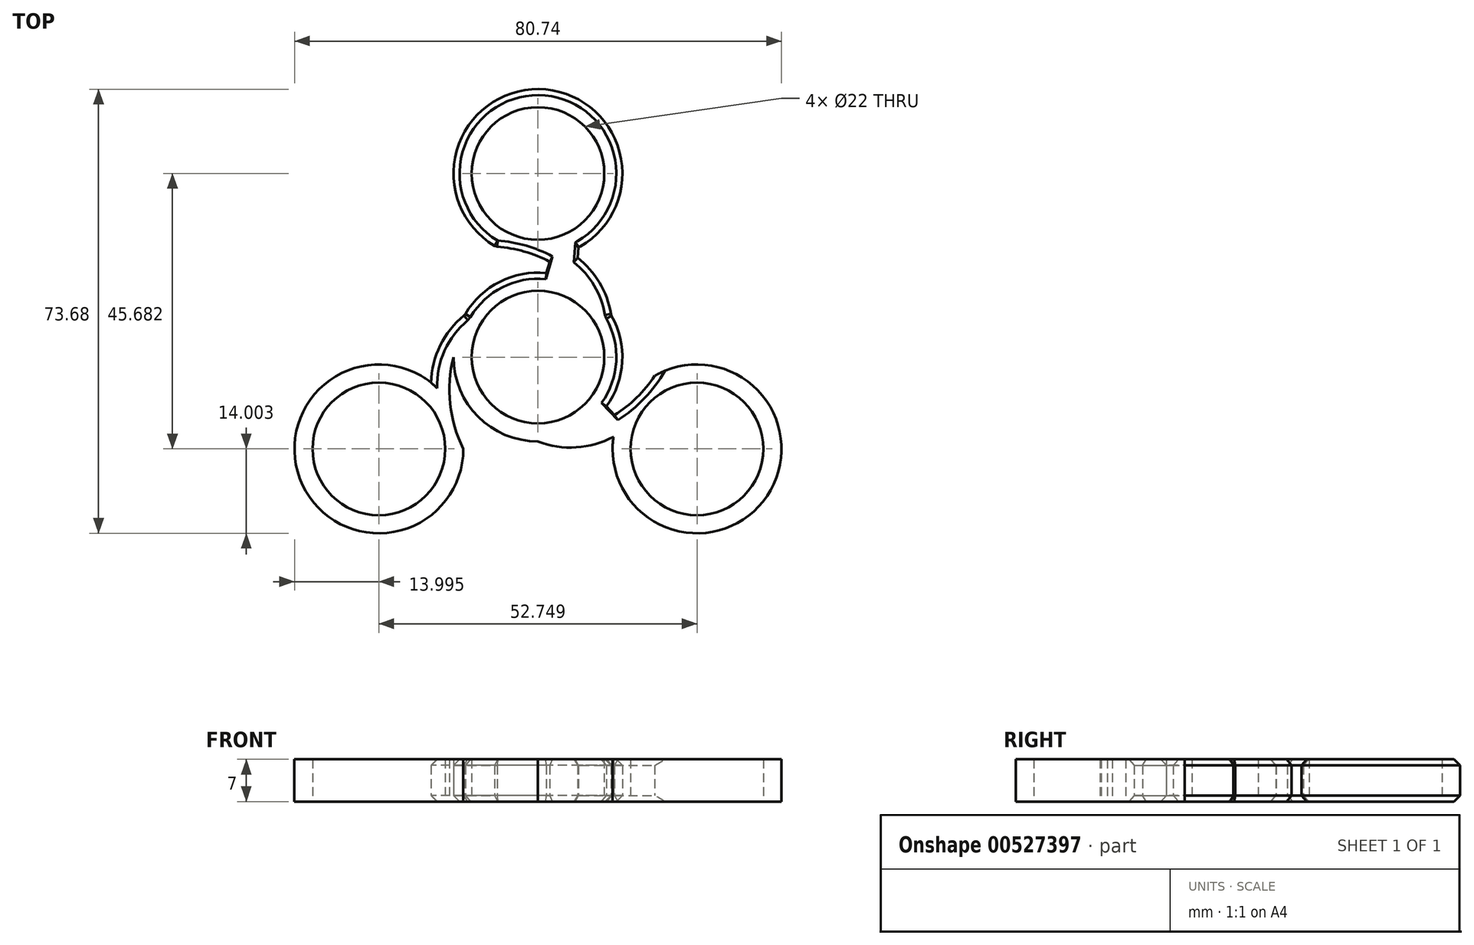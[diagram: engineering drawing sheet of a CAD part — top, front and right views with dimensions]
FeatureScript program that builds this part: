
annotation { "Feature Type Name" : "Feature", "Feature Type Description" : "" }
export const myFeature = defineFeature(function(context is Context, id is Id, definition is map)
    precondition{}
    {
        {
            var Q0;
            Q0=qCreatedBy(makeId("Top.planeOp"),FACE);
            var sketch = newSketch(context, id + "F0", { "sketchPlane" : qUnion([Q0])});
            skCircle(sketch, "E0", {"center": v(0, 0) * mm, "radius": 11 * mm});
            skArc(sketch, "E1.0", {"start": v(7, 12.12) * mm, "mid": v(-9.9, 9.9) * mm, "end": v(-12.12, -7) * mm});
            skCircle(sketch, "E2", {"center": v(0, 30.45) * mm, "radius": 11 * mm});
            skArc(sketch, "E3.0", {"start": v(7, 18.33) * mm, "mid": v(0, 44.45) * mm, "end": v(-7, 18.33) * mm});
            skLineSegment(sketch, "E4", {"start": v(0, 30.45) * mm, "end": v(-5.5, 20.93) * mm});
            skLineSegment(sketch, "E5", {"start": v(0, 19.45) * mm, "end": v(0, 30.45) * mm});
            skLineSegment(sketch, "E6.MirrorCS", {"start": v(0, 30.45) * mm, "end": v(5.5, 20.93) * mm});
            skLineSegment(sketch, "E7", {"start": v(0, 19.45) * mm, "end": v(0, 16.73) * mm});
            skPoint(sketch, "E8", {"position": v(0, 16.73) * mm});
            skLineSegment(sketch, "E9", {"start": v(0, 0) * mm, "end": v(7, 12.12) * mm});
            skArc(sketch, "E10", {"start": v(7, 12.12) * mm, "mid": v(0.56, 16.49) * mm, "end": v(-7, 18.33) * mm});
            skLineSegment(sketch, "E11", {"start": v(0, 0) * mm, "end": v(12.12, 7) * mm});
            skArc(sketch, "E12", {"start": v(12.12, 7) * mm, "mid": v(9.8, 13) * mm, "end": v(5.17, 17.47) * mm});
            skArc(sketch, "E13", {"start": v(7, 18.33) * mm, "mid": v(6.1, 17.86) * mm, "end": v(5.17, 17.47) * mm});
            skPoint(sketch, "E14.orphan", {"position": v(0, 14) * mm});
            skPoint(sketch, "E15.MirrorCS.start.orphan", {"position": v(12.12, -7) * mm});
            skPoint(sketch, "E16.orphan", {"position": v(7, -12.12) * mm});
            skArc(sketch, "E17.trimOffspring", {"start": v(-7, -12.12) * mm, "mid": v(9.9, -9.9) * mm, "end": v(12.12, 7) * mm});
            skArc(sketch, "E18", {"start": v(-12.12, -7) * mm, "mid": v(-9.9, -9.9) * mm, "end": v(-7, -12.12) * mm});
            skArc(sketch, "E19.1.0", {"start": v(-12.12, 7) * mm, "mid": v(-16.15, 1.99) * mm, "end": v(-17.71, -4.25) * mm});
            skArc(sketch, "E19.1.1", {"start": v(-14, 0) * mm, "mid": v(-14.56, -7.76) * mm, "end": v(-12.37, -15.23) * mm});
            skArc(sketch, "E19.1.2", {"start": v(-19.37, -3.1) * mm, "mid": v(-38.5, -22.23) * mm, "end": v(-12.37, -15.23) * mm});
            skCircle(sketch, "E19.1.3", {"center": v(-26.37, -15.23) * mm, "radius": 11 * mm});
            skArc(sketch, "E19.1.4", {"start": v(-19.37, -3.1) * mm, "mid": v(-18.52, -3.64) * mm, "end": v(-17.71, -4.25) * mm});
            skArc(sketch, "E19.2.0", {"start": v(0, -14) * mm, "mid": v(6.36, -14.98) * mm, "end": v(12.54, -13.21) * mm});
            skArc(sketch, "E19.2.1", {"start": v(7, -12.12) * mm, "mid": v(14, -8.73) * mm, "end": v(19.37, -3.1) * mm});
            skArc(sketch, "E19.2.2", {"start": v(12.37, -15.23) * mm, "mid": v(38.5, -22.23) * mm, "end": v(19.37, -3.1) * mm});
            skCircle(sketch, "E19.2.3", {"center": v(26.37, -15.23) * mm, "radius": 11 * mm});
            skArc(sketch, "E19.2.4", {"start": v(12.37, -15.23) * mm, "mid": v(12.42, -14.22) * mm, "end": v(12.54, -13.21) * mm});
            skSolve(sketch);
        }
        {
            var Q0;
            {var subQ4=sQuery(id+"F0.wireOp",EDGE,"E1.0");Q0=makeQuery(id+"F0.imprint","IMPRINT",FACE,{"disambiguationData":[TD([[makeQuery(id+"F0.imprint","IMPRINT",EDGE,{"derivedFrom":subQ4}),1.0]])]});}
            var Q1;
            {var subQ1=sQuery(id+"F0.wireOp",EDGE,"E3.0");Q1=makeQuery(id+"F0.imprint","IMPRINT",FACE,{"disambiguationData":[TD([[makeQuery(id+"F0.imprint","IMPRINT",EDGE,{"derivedFrom":subQ1}),1.0]])]});}
            var Q2;
            {var subQ1=sQuery(id+"F0.wireOp",EDGE,"E19.1.0");Q2=makeQuery(id+"F0.imprint","IMPRINT",FACE,{"disambiguationData":[TD([[makeQuery(id+"F0.imprint","IMPRINT",EDGE,{"derivedFrom":subQ1}),1.0]])]});}
            var Q3;
            {var subQ1=sQuery(id+"F0.wireOp",EDGE,"E19.2.0");Q3=makeQuery(id+"F0.imprint","IMPRINT",FACE,{"disambiguationData":[TD([[makeQuery(id+"F0.imprint","IMPRINT",EDGE,{"derivedFrom":subQ1}),1.0]])]});}
            extrude(context, id + "F1", {"entities" : qUnion([Q0, Q1, Q2, Q3]), "endBound" : BoundingType.SYMMETRIC, "depth" : 7 * mm, "offsetDistance" : 25 * mm});
        }
        {
            var Q0;
            Q0=makeQuery(id+"F1.opExtrude","SWEPT_FACE",FACE,{"disambiguationData":[OSD([sQuery(id+"F0.wireOp",EDGE,"a974154c-ccaf-4894-bf03-dca1b5e2c5db0.MirrorCS")])]});
            var Q1;
            Q1=makeQuery(id+"F1.opExtrude","SWEPT_FACE",FACE,{"disambiguationData":[OSD([sQuery(id+"F0.wireOp",EDGE,"E17.trimOffspring")])]});
            var Q2;
            Q2=makeQuery(id+"F1.opExtrude","SWEPT_FACE",FACE,{"disambiguationData":[OSD([sQuery(id+"F0.wireOp",EDGE,"E12")])]});
            var Q3;
            Q3=makeQuery(id+"F1.opExtrude","SWEPT_FACE",FACE,{"disambiguationData":[OSD([sQuery(id+"F0.wireOp",EDGE,"E3.0")])]});
            var Q4;
            Q4=makeQuery(id+"F1.opExtrude","SWEPT_FACE",FACE,{"disambiguationData":[OSD([sQuery(id+"F0.wireOp",EDGE,"E1.0")])]});
            var Q5;
            Q5=makeQuery(id+"F1.opExtrude","SWEPT_FACE",FACE,{"disambiguationData":[OSD([sQuery(id+"F0.wireOp",EDGE,"1ae71e8a-6735-4fb3-9f52-99f22391f5f40.MirrorCS")])]});
            chamfer(context, id + "F2", {"entities" : qUnion([Q0, Q1, Q2, Q3, Q4, Q5]), "width" : 1 * mm, "tangentPropagation" : true});
        }
    });
